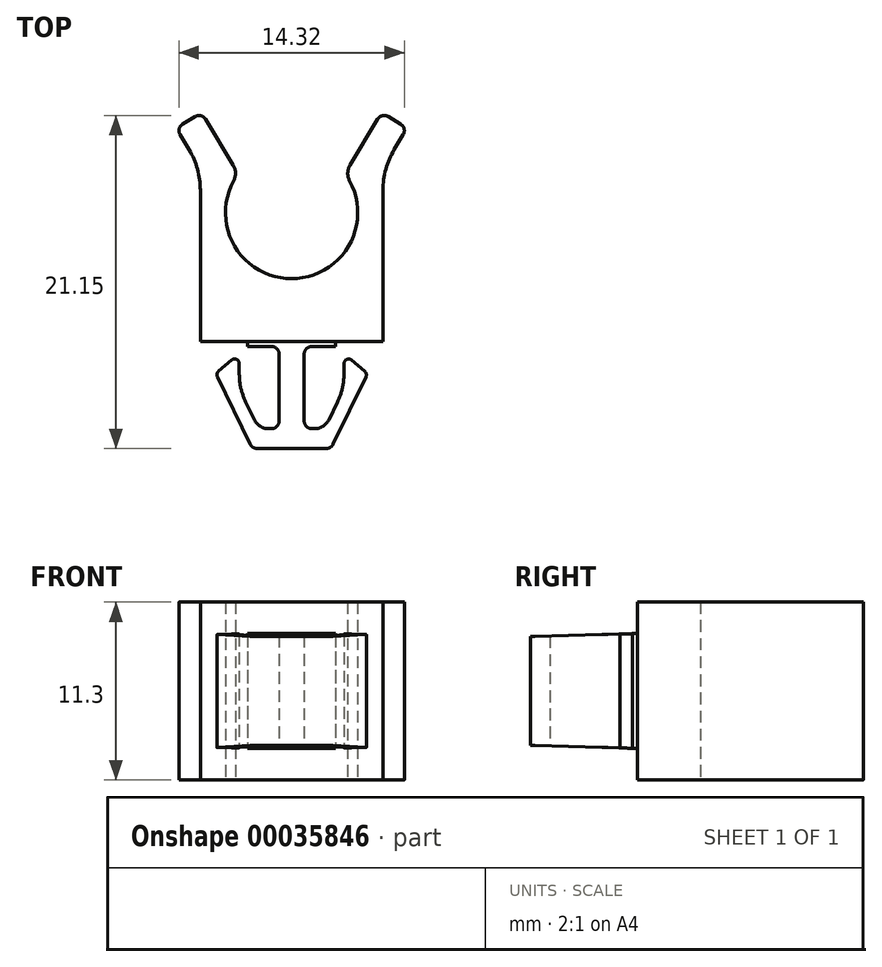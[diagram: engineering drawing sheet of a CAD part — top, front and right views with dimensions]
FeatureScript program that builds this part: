
annotation { "Feature Type Name" : "Feature", "Feature Type Description" : "" }
export const myFeature = defineFeature(function(context is Context, id is Id, definition is map)
    precondition{}
    {
        {
            var Q0;
            Q0=qCreatedBy(makeId("Top.planeOp"),FACE);
            var sketch = newSketch(context, id + "F0", { "sketchPlane" : qUnion([Q0])});
            skLineSegment(sketch, "E0", {"start": v(-5.8, 0) * mm, "end": v(-5.8, 9.62) * mm});
            skLineSegment(sketch, "E1", {"start": v(-6.51, 12.19) * mm, "end": v(-7.08, 13.14) * mm});
            skLineSegment(sketch, "E2", {"start": v(-5.46, 14.12) * mm, "end": v(-3.7, 11.2) * mm});
            skLineSegment(sketch, "E3", {"start": v(-6.91, 13.83) * mm, "end": v(-6.14, 14.3) * mm});
            skLineSegment(sketch, "E4", {"start": v(-5.8, 0) * mm, "end": v(0, 0) * mm});
            skArc(sketch, "E5", {"start": v(-3.69, 10.21) * mm, "mid": v(-3.61, 6.06) * mm, "end": v(0, 4) * mm});
            skLineSegment(sketch, "E6.bottom", {"start": v(0, 0) * mm, "end": v(-2.8, 0) * mm});
            skLineSegment(sketch, "E6.right", {"start": v(-2.8, 0) * mm, "end": v(-2.8, -0.3) * mm});
            skLineSegment(sketch, "E7", {"start": v(-2.64, -6.5) * mm, "end": v(-4.71, -2.23) * mm});
            skLineSegment(sketch, "E8", {"start": v(-5.8, 0) * mm, "end": v(-2.5, -6.8) * mm, "construction": true});
            skLineSegment(sketch, "E9", {"start": v(-4.64, -1.87) * mm, "end": v(-3.82, -1.17) * mm});
            skLineSegment(sketch, "E10", {"start": v(-3.32, -1.4) * mm, "end": v(-3.32, -2.07) * mm});
            skLineSegment(sketch, "E11", {"start": v(-2.92, -3.82) * mm, "end": v(-2.36, -4.97) * mm});
            skLineSegment(sketch, "E12", {"start": v(-4.82, -2.02) * mm, "end": v(-2.8, -0.3) * mm, "construction": true});
            skLineSegment(sketch, "E13.MirrorCS", {"start": v(2.8, 0) * mm, "end": v(2.8, -0.3) * mm});
            skPoint(sketch, "E14.visualSharp", {"position": v(-5.8, 11) * mm});
            skArc(sketch, "E14.filletArc", {"start": v(-5.8, 9.62) * mm, "mid": v(-5.98, 10.95) * mm, "end": v(-6.51, 12.19) * mm});
            skLineSegment(sketch, "E15", {"start": v(-2.8, -0.3) * mm, "end": v(-1.3, -0.3) * mm});
            skLineSegment(sketch, "E16", {"start": v(-1.46, -5.53) * mm, "end": v(-1.3, -5.53) * mm});
            skLineSegment(sketch, "E17", {"start": v(-0.8, -5.03) * mm, "end": v(-0.8, -0.8) * mm});
            skLineSegment(sketch, "E18", {"start": v(-2.19, -6.8) * mm, "end": v(0, -6.8) * mm});
            skPoint(sketch, "E19.visualSharp", {"position": v(-3.32, -3) * mm});
            skArc(sketch, "E19.filletArc", {"start": v(-3.32, -2.07) * mm, "mid": v(-3.22, -2.97) * mm, "end": v(-2.92, -3.82) * mm});
            skPoint(sketch, "E20.visualSharp", {"position": v(-3.32, -0.75) * mm});
            skArc(sketch, "E20.filletArc", {"start": v(-3.32, -1.4) * mm, "mid": v(-3.5, -1.13) * mm, "end": v(-3.82, -1.17) * mm});
            skPoint(sketch, "E21.visualSharp", {"position": v(-4.82, -2.02) * mm});
            skArc(sketch, "E21.filletArc", {"start": v(-4.64, -1.87) * mm, "mid": v(-4.74, -2.04) * mm, "end": v(-4.71, -2.23) * mm});
            skPoint(sketch, "E22.visualSharp", {"position": v(-2.09, -5.53) * mm});
            skArc(sketch, "E22.filletArc", {"start": v(-2.36, -4.97) * mm, "mid": v(-2, -5.38) * mm, "end": v(-1.46, -5.53) * mm});
            skPoint(sketch, "E23.visualSharp", {"position": v(-0.8, -0.3) * mm});
            skArc(sketch, "E23.filletArc", {"start": v(-0.8, -0.8) * mm, "mid": v(-0.94, -0.45) * mm, "end": v(-1.3, -0.3) * mm});
            skPoint(sketch, "E24.visualSharp", {"position": v(-5.71, 14.55) * mm});
            skArc(sketch, "E24.filletArc", {"start": v(-5.46, 14.12) * mm, "mid": v(-5.76, 14.35) * mm, "end": v(-6.14, 14.3) * mm});
            skPoint(sketch, "E25.visualSharp", {"position": v(-7.34, 13.57) * mm});
            skArc(sketch, "E25.filletArc", {"start": v(-6.91, 13.83) * mm, "mid": v(-7.14, 13.52) * mm, "end": v(-7.08, 13.14) * mm});
            skPoint(sketch, "E26.visualSharp", {"position": v(-3.4, 10.68) * mm});
            skArc(sketch, "E26.filletArc", {"start": v(-3.69, 10.21) * mm, "mid": v(-3.57, 10.71) * mm, "end": v(-3.7, 11.2) * mm});
            skPoint(sketch, "E27.visualSharp", {"position": v(-2.5, -6.8) * mm});
            skArc(sketch, "E27.filletArc", {"start": v(-2.64, -6.5) * mm, "mid": v(-2.45, -6.71) * mm, "end": v(-2.19, -6.8) * mm});
            skPoint(sketch, "E28.visualSharp", {"position": v(-0.8, -5.53) * mm});
            skArc(sketch, "E28.filletArc", {"start": v(-1.3, -5.53) * mm, "mid": v(-0.94, -5.39) * mm, "end": v(-0.8, -5.03) * mm});
            skArc(sketch, "E29.MirrorCS", {"start": v(3.69, 10.21) * mm, "mid": v(3.61, 6.06) * mm, "end": v(0, 4) * mm});
            skArc(sketch, "E30.MirrorCS", {"start": v(3.69, 10.21) * mm, "mid": v(3.57, 10.71) * mm, "end": v(3.7, 11.2) * mm});
            skLineSegment(sketch, "E31.MirrorCS", {"start": v(5.46, 14.12) * mm, "end": v(3.7, 11.2) * mm});
            skArc(sketch, "E32.MirrorCS", {"start": v(5.46, 14.12) * mm, "mid": v(5.76, 14.35) * mm, "end": v(6.14, 14.3) * mm});
            skLineSegment(sketch, "E33.MirrorCS", {"start": v(6.91, 13.83) * mm, "end": v(6.14, 14.3) * mm});
            skArc(sketch, "E34.MirrorCS", {"start": v(6.91, 13.83) * mm, "mid": v(7.14, 13.52) * mm, "end": v(7.08, 13.14) * mm});
            skLineSegment(sketch, "E35.MirrorCS", {"start": v(6.51, 12.19) * mm, "end": v(7.08, 13.14) * mm});
            skArc(sketch, "E36.MirrorCS", {"start": v(5.8, 9.62) * mm, "mid": v(5.98, 10.95) * mm, "end": v(6.51, 12.19) * mm});
            skLineSegment(sketch, "E37.MirrorCS", {"start": v(5.8, 0) * mm, "end": v(5.8, 9.62) * mm});
            skLineSegment(sketch, "E38.MirrorCS", {"start": v(2.8, -0.3) * mm, "end": v(1.3, -0.3) * mm});
            skArc(sketch, "E39.MirrorCS", {"start": v(0.8, -0.8) * mm, "mid": v(0.94, -0.45) * mm, "end": v(1.3, -0.3) * mm});
            skLineSegment(sketch, "E40.MirrorCS", {"start": v(0.8, -5.03) * mm, "end": v(0.8, -0.8) * mm});
            skArc(sketch, "E41.MirrorCS", {"start": v(1.3, -5.53) * mm, "mid": v(0.94, -5.39) * mm, "end": v(0.8, -5.03) * mm});
            skLineSegment(sketch, "E42.MirrorCS", {"start": v(1.46, -5.53) * mm, "end": v(1.3, -5.53) * mm});
            skArc(sketch, "E43.MirrorCS", {"start": v(2.36, -4.97) * mm, "mid": v(2, -5.38) * mm, "end": v(1.46, -5.53) * mm});
            skLineSegment(sketch, "E44.MirrorCS", {"start": v(2.92, -3.82) * mm, "end": v(2.36, -4.97) * mm});
            skArc(sketch, "E45.MirrorCS", {"start": v(3.32, -2.07) * mm, "mid": v(3.22, -2.97) * mm, "end": v(2.92, -3.82) * mm});
            skLineSegment(sketch, "E46.MirrorCS", {"start": v(3.32, -1.4) * mm, "end": v(3.32, -2.07) * mm});
            skArc(sketch, "E47.MirrorCS", {"start": v(3.32, -1.4) * mm, "mid": v(3.5, -1.13) * mm, "end": v(3.82, -1.17) * mm});
            skLineSegment(sketch, "E48.MirrorCS", {"start": v(4.64, -1.87) * mm, "end": v(3.82, -1.17) * mm});
            skArc(sketch, "E49.MirrorCS", {"start": v(4.64, -1.87) * mm, "mid": v(4.74, -2.04) * mm, "end": v(4.71, -2.23) * mm});
            skLineSegment(sketch, "E50.MirrorCS", {"start": v(2.64, -6.5) * mm, "end": v(4.71, -2.23) * mm});
            skArc(sketch, "E51.MirrorCS", {"start": v(2.64, -6.5) * mm, "mid": v(2.45, -6.71) * mm, "end": v(2.19, -6.8) * mm});
            skLineSegment(sketch, "E52.MirrorCS", {"start": v(2.19, -6.8) * mm, "end": v(0, -6.8) * mm});
            skLineSegment(sketch, "E53.MirrorCS", {"start": v(5.8, 0) * mm, "end": v(0, 0) * mm});
            skSolve(sketch);
        }
        {
            var Q0;
            Q0 = qSketchRegion(id + "F0", true);
            extrude(context, id + "F1", {"entities" : qUnion([Q0]), "depth" : 11.3 * mm});
        }
        {
            var Q0;
            Q0=qCreatedBy(makeId("Right.planeOp"),FACE);
            var sketch = newSketch(context, id + "F2", { "sketchPlane" : qUnion([Q0])});
            skLineSegment(sketch, "E54", {"start": v(0, 0) * mm, "end": v(0, 2) * mm});
            skLineSegment(sketch, "E55", {"start": v(0, 2) * mm, "end": v(-6.8, 2.2) * mm});
            skLineSegment(sketch, "E56", {"start": v(-6.8, 2.2) * mm, "end": v(-6.8, 0) * mm});
            skLineSegment(sketch, "E57", {"start": v(-6.8, 0) * mm, "end": v(0, 0) * mm});
            skLineSegment(sketch, "E58", {"start": v(-6.8, 5.65) * mm, "end": v(14.3, 5.65) * mm, "construction": true});
            skLineSegment(sketch, "E59.MirrorCS", {"start": v(0, 9.3) * mm, "end": v(-6.8, 9.1) * mm});
            skLineSegment(sketch, "E60.MirrorCS", {"start": v(0, 11.3) * mm, "end": v(0, 9.3) * mm});
            skLineSegment(sketch, "E61.MirrorCS", {"start": v(-6.8, 11.3) * mm, "end": v(0, 11.3) * mm});
            skLineSegment(sketch, "E62.MirrorCS", {"start": v(-6.8, 9.1) * mm, "end": v(-6.8, 11.3) * mm});
            skSolve(sketch);
        }
        {
            var Q0;
            Q0 = qSketchRegion(id + "F2", true);
            extrude(context, id + "F3", {"entities" : qUnion([Q0]), "operationType" : NewBodyOperationType.REMOVE, "endBound" : BoundingType.SYMMETRIC, "oppositeDirection" : true, "depth" : 12 * mm});
        }
    });
